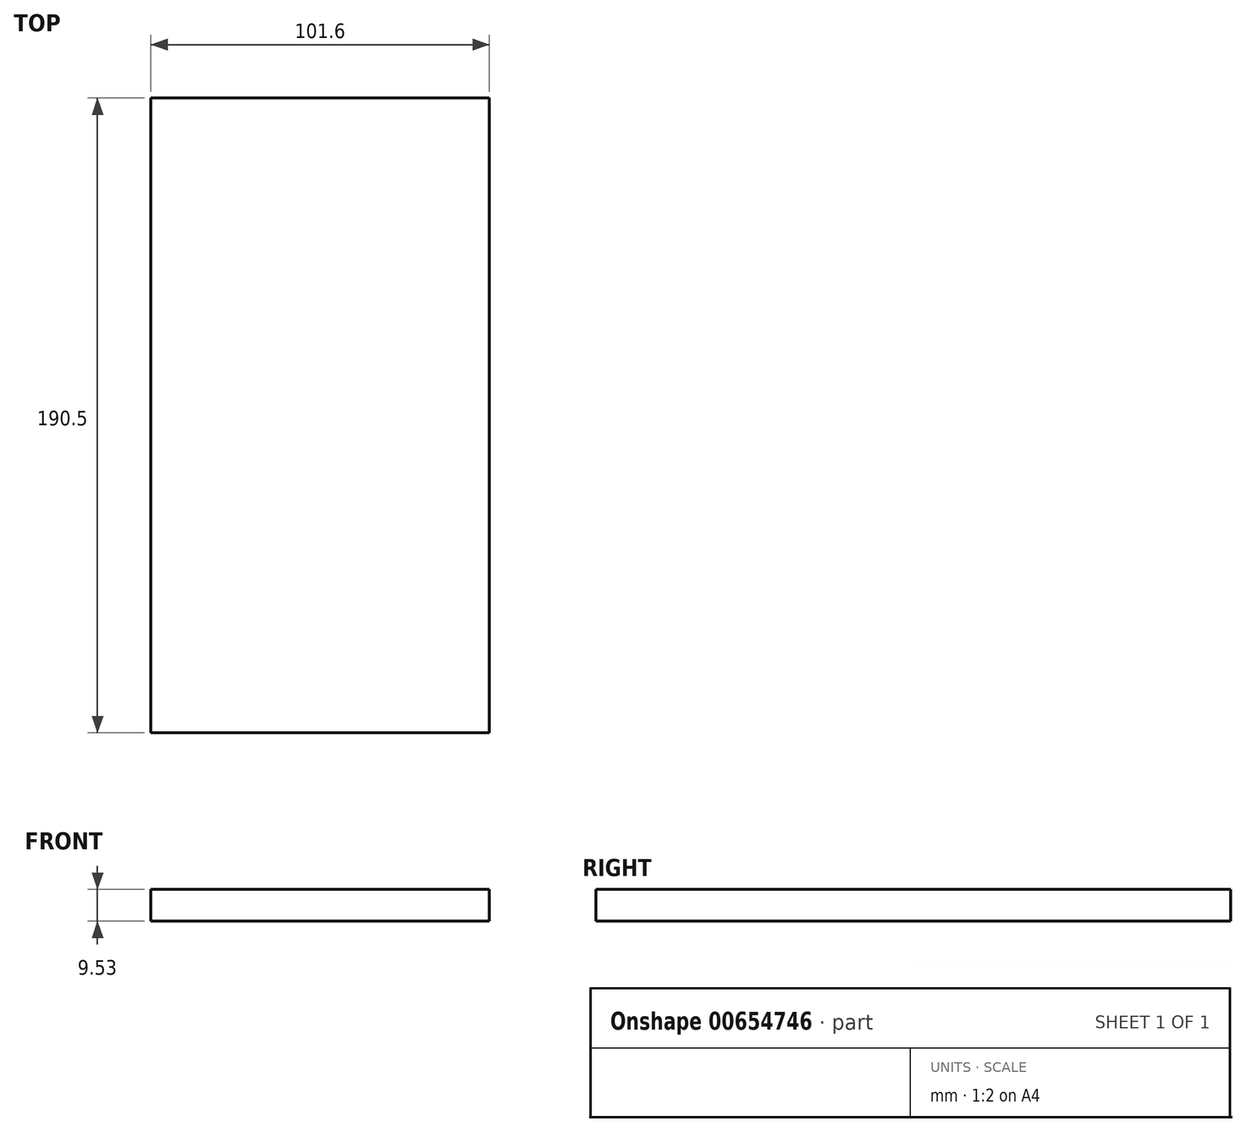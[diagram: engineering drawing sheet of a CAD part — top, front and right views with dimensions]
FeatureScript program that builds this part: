
annotation { "Feature Type Name" : "Feature", "Feature Type Description" : "" }
export const myFeature = defineFeature(function(context is Context, id is Id, definition is map)
    precondition{}
    {
        {
            var Q0;
            Q0=qCreatedBy(makeId("Top.planeOp"),FACE);
            var sketch = newSketch(context, id + "F0", { "sketchPlane" : qUnion([Q0])});
            skLineSegment(sketch, "E0.bottom", {"start": v(-129.52, -170.53) * mm, "end": v(-27.92, -170.53) * mm});
            skLineSegment(sketch, "E0.top", {"start": v(-129.52, 19.97) * mm, "end": v(-27.92, 19.97) * mm});
            skLineSegment(sketch, "E0.left", {"start": v(-129.52, -170.53) * mm, "end": v(-129.52, 19.97) * mm});
            skLineSegment(sketch, "E0.right", {"start": v(-27.92, -170.53) * mm, "end": v(-27.92, 19.97) * mm});
            skLineSegment(sketch, "E1.direction1", {"start": v(-116.82, 19.97) * mm, "end": v(-40.62, 19.97) * mm, "construction": true});
            skSolve(sketch);
        }
        {
            var Q0;
            Q0=makeQuery(id+"F0.imprint","IMPRINT",FACE,{"disambiguationData":[TD([[makeQuery(id+"F0.imprint","IMPRINT",EDGE,{"derivedFrom":sQuery(id+"F0.wireOp",EDGE,"E0.bottom")}),1.0]])]});
            extrude(context, id + "F1", {"entities" : qUnion([Q0]), "depth" : 9.52 * mm, "offsetDistance" : 25.4 * mm});
        }
    });
